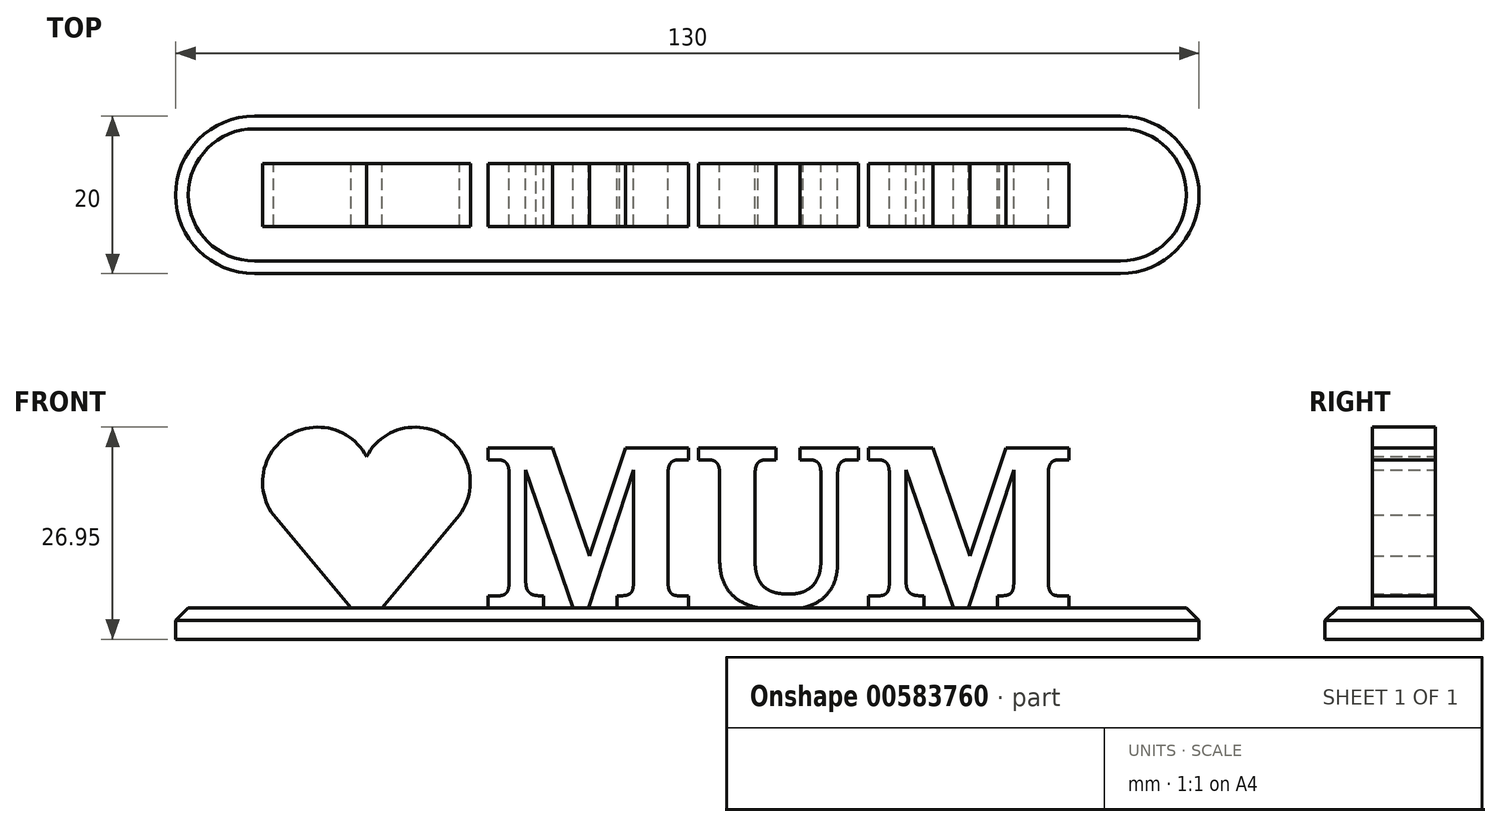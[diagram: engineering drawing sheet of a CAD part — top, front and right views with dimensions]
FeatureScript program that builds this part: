
annotation { "Feature Type Name" : "Feature", "Feature Type Description" : "" }
export const myFeature = defineFeature(function(context is Context, id is Id, definition is map)
    precondition{}
    {
        {
            var Q0;
            Q0=qCreatedBy(makeId("Top.planeOp"),FACE);
            var sketch = newSketch(context, id + "F0", { "sketchPlane" : qUnion([Q0])});
            skLineSegment(sketch, "E0.bottom", {"start": v(0, 0) * mm, "end": v(130, 0) * mm});
            skLineSegment(sketch, "E0.top", {"start": v(0, 20) * mm, "end": v(130, 20) * mm});
            skLineSegment(sketch, "E0.left", {"start": v(0, 0) * mm, "end": v(0, 20) * mm});
            skLineSegment(sketch, "E0.right", {"start": v(130, 0) * mm, "end": v(130, 20) * mm});
            skSolve(sketch);
        }
        {
            var Q0;
            Q0 = qSketchRegion(id + "F0", true);
            extrude(context, id + "F1", {"entities" : qUnion([Q0]), "depth" : 4 * mm, "offsetDistance" : 25 * mm});
        }
        {
            var Q0;
            Q0=qCreatedBy(makeId("Front.planeOp"),FACE);
            cPlane(context, id + "F2", {"entities" : qUnion([Q0]), "cplaneType" : CPlaneType.OFFSET, "offset" : 10 * mm, "oppositeDirection" : true, "width" : 150 * mm, "height" : 150 * mm});
        }
        {
            var Q0;
            Q0=qCreatedBy(id+"F2.planeOp",FACE);
            var sketch = newSketch(context, id + "F3", { "sketchPlane" : qUnion([Q0])});
            skPoint(sketch, "E1.0", {"position": v(0, 4) * mm});
            skPoint(sketch, "E2.0", {"position": v(65, 4) * mm});
            skLineSegment(sketch, "E3.bottom", {"start": v(65, 4) * mm, "end": v(14.7, 4) * mm});
            skLineSegment(sketch, "E3.left", {"start": v(65, 4) * mm, "end": v(65, 26.95) * mm, "construction": true});
            skLineSegment(sketch, "E4.MirrorCS", {"start": v(115.3, 4) * mm, "end": v(115.3, 26.95) * mm});
            skLineSegment(sketch, "E5.MirrorCS", {"start": v(65, 4) * mm, "end": v(115.3, 4) * mm});
            skLineSegment(sketch, "E6", {"start": v(-5.35, 19.95) * mm, "end": v(105.87, 19.95) * mm, "construction": true});
            skArc(sketch, "E7", {"start": v(24.23, 23.2) * mm, "mid": v(13.97, 25.64) * mm, "end": v(12.94, 15.15) * mm});
            skArc(sketch, "E8", {"start": v(35.52, 15.15) * mm, "mid": v(34.5, 25.64) * mm, "end": v(24.23, 23.2) * mm});
            skLineSegment(sketch, "E9", {"start": v(12.42, 15.77) * mm, "end": v(22.27, 4) * mm});
            skLineSegment(sketch, "E10", {"start": v(24.23, 23.2) * mm, "end": v(24.23, 4) * mm, "construction": true});
            skLineSegment(sketch, "E11.MirrorCS", {"start": v(36.04, 15.77) * mm, "end": v(26.19, 4) * mm});
            skPoint(sketch, "E12.orphan", {"position": v(14.7, 26.95) * mm});
            skText(sketch, "E13", { "text": "MUM", "fontName": "NotoSerif-Bold.ttf"});
            skPoint(sketch, "E14.MirrorCS.end.orphan", {"position": v(115.3, 26.95) * mm});
            skPoint(sketch, "E14.MirrorCS.start.orphan", {"position": v(65, 26.95) * mm});
            const initialGuessF3  = {"E13": [0.0389, 0.004, 1, 0, 0.02047]};
            skSetInitialGuess(sketch, initialGuessF3);
            skSolve(sketch);
        }
        {
            var Q0;
            {var subQ0=sQuery(id+"F3.wireOp",EDGE,"E9");var subQ8=sQuery(id+"F3.wireOp",EDGE,"E3.bottom");var subQ9=makeQuery(id+"F3.imprint","INTERSECT",VERTEX,{"derivedFrom":[subQ8,subQ0]});Q0=makeQuery(id+"F3.imprint","IMPRINT",FACE,{"disambiguationData":[TD([[makeQuery(id+"F3.imprint","IMPRINT",EDGE,{"disambiguationData":[TD([[subQ9,1.0]])],"derivedFrom":subQ8}),-1.0]])]});}
            var Q1;
            Q1=makeQuery(id+"F3.imprint","IMPRINT",FACE,{"disambiguationData":[TD([[makeQuery(id+"F3.imprint","IMPRINT",EDGE,{"derivedFrom":sQuery(id+"F3.wireOp",EDGE,"E13.sketch_text.stroke-0")}),-1.0]])]});
            var Q2;
            Q2=makeQuery(id+"F3.imprint","IMPRINT",FACE,{"disambiguationData":[TD([[makeQuery(id+"F3.imprint","IMPRINT",EDGE,{"derivedFrom":sQuery(id+"F3.wireOp",EDGE,"E13.sketch_text.stroke-49")}),-1.0]])]});
            var Q3;
            Q3=makeQuery(id+"F3.imprint","IMPRINT",FACE,{"disambiguationData":[TD([[makeQuery(id+"F3.imprint","IMPRINT",EDGE,{"derivedFrom":sQuery(id+"F3.wireOp",EDGE,"E13.sketch_text.stroke-95")}),-1.0]])]});
            extrude(context, id + "F4", {"entities" : qUnion([Q0, Q1, Q2, Q3]), "operationType" : NewBodyOperationType.ADD, "depth" : 4 * mm, "offsetDistance" : 25 * mm, "hasSecondDirection" : true, "secondDirectionOppositeDirection" : true, "secondDirectionDepth" : 4 * mm});
        }
        {
            var Q0;
            Q0=makeQuery(id+"F1.opExtrude","SWEPT_EDGE",EDGE,{"disambiguationData":[OSD([sQuery(id+"F0.wireOp",EDGE,"E0.bottom"),sQuery(id+"F0.wireOp",EDGE,"E0.left")])]});
            var Q1;
            Q1=makeQuery(id+"F1.opExtrude","SWEPT_EDGE",EDGE,{"disambiguationData":[OSD([sQuery(id+"F0.wireOp",EDGE,"E0.top"),sQuery(id+"F0.wireOp",EDGE,"E0.left")])]});
            var Q2;
            Q2=makeQuery(id+"F1.opExtrude","SWEPT_EDGE",EDGE,{"disambiguationData":[OSD([sQuery(id+"F0.wireOp",EDGE,"E0.bottom"),sQuery(id+"F0.wireOp",EDGE,"E0.right")])]});
            var Q3;
            Q3=makeQuery(id+"F1.opExtrude","SWEPT_EDGE",EDGE,{"disambiguationData":[OSD([sQuery(id+"F0.wireOp",EDGE,"E0.top"),sQuery(id+"F0.wireOp",EDGE,"E0.right")])]});
            fillet(context, id + "F5", {"entities" : qUnion([Q0, Q1, Q2, Q3]), "radius" : 10 * mm, "tangentPropagation" : true, "allowEdgeOverflow" : false});
        }
        {
            var Q0;
            {var subQ0=sQuery(id+"F0.wireOp",EDGE,"E0.left");var subQ1=sQuery(id+"F0.wireOp",EDGE,"E0.bottom");Q0=makeQuery(id+"F5.opFillet","BLEND_EDGE",EDGE,{"blendedFrom":[makeQuery(id+"F1.opExtrude","SWEPT_EDGE",EDGE,{"disambiguationData":[OSD([subQ1,subQ0])]}),makeQuery(id+"F1.opExtrude","CAP_FACE",FACE,{"disambiguationData":[OSD([subQ1,sQuery(id+"F0.wireOp",EDGE,"E0.top"),subQ0,sQuery(id+"F0.wireOp",EDGE,"E0.right")])],"isStart":false})],"blendedInto":[makeQuery(id+"F1.opExtrude","CAP_FACE",FACE,{"disambiguationData":[OSD([subQ1,sQuery(id+"F0.wireOp",EDGE,"E0.top"),subQ0,sQuery(id+"F0.wireOp",EDGE,"E0.right")])],"isStart":false})]});}
            chamfer(context, id + "F6", {"entities" : qUnion([Q0]), "width" : 1.6 * mm, "tangentPropagation" : true});
        }
    });
